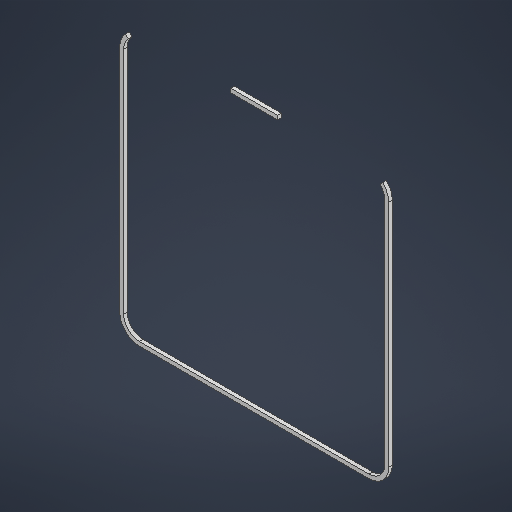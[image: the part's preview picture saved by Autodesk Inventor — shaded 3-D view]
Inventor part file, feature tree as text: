
AUTODESK INVENTOR PART (.ipt)
format: ipt  version: 2025 (Build 290162000, 162)  size: 233,984 bytes
history: native  units: mm
features: other x1, extrude x1, sketch x1
ambient origin geometry x8: Origin, YZ Plane, XZ Plane, XY Plane, X Axis, Y Axis, Z Axis, Center Point
bodies: Body1 (feature_tree)
feature tree (3):
  other  "Těleso1"
  extrude  "Vysunutí1"  Depth=109.0mm
  sketch  "Náčrt1"
